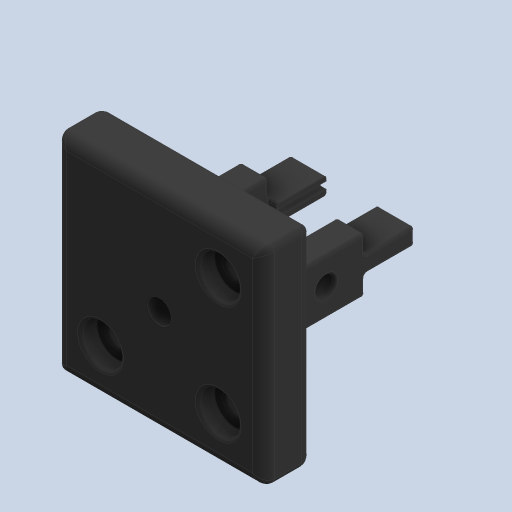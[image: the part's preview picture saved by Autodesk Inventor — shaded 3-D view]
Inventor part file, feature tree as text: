
AUTODESK INVENTOR PART (.ipt)
format: ipt  version: 2023 (Build 270158000, 158)  size: 980,992 bytes
history: native  units: mm
features: other x13, extrude x13, fillet x6, chamfer x4, sketch x3, mirror x1, projected_geometry x1
ambient origin geometry x8: Origin, YZ Plane, XZ Plane, XY Plane, X Axis, Y Axis, Z Axis, Center Point
bodies: Solid1 (feature_tree)
feature tree (41):
  other  "NP2-Alpha_Payload.ipt"
  other  "Universal_ConstructorHead.ipt"
  other  "Sk:SideArmSlot"
  extrude  "Ex:SideArmSlot"  Depth=9.0mm TaperAngle=0.0deg
  extrude  "Ex:SideArmExtension"  TaperAngle=0.0deg  [1 undecoded]
  other  "Sk:LateralFeatures"
  extrude  "Ex:TopConnection"  Depth=1.0mm
  extrude  "Ex:ThreadProtrusion"  Depth=1.0mm
  fillet  "Fillet:Protrusion"  Radius=6.5mm
  fillet  "Fillet:AllOfArm"  Radius=1.0mm
  extrude  "Ex:ScrewHole"  Depth=10.0mm
  extrude  "Ex:InterArmExtend"  Depth=1.0mm TaperAngle=0.0deg
  other  "Move:InterArmExtend"
  mirror  "Mirror1"
  extrude  "Ex:ThreadInsert"  Depth=9.0mm TaperAngle=0.0deg
  chamfer  "Chamfer:ThreadInsertOpt1"  Distance=10.0mm
  chamfer  "Chamfer:ThreadInsertOpt2"  Distance=3.0mm
  fillet  "Fillet:ThroughHoleOpt1"  Radius=6.5mm
  fillet  "Fillet:ThroughHoleOpt2"  Radius=6.5mm
  other  "TopPlane"
  other  "Sk:TopExpansion"
  fillet  "Fillet:TopCorner"  Radius=6.5mm
  extrude  "Ex:MainTopBody"  Depth=1.0mm
  extrude  "Ex:CavitiesForPosts"  Depth=10.0mm
  extrude  "Ex:TopThread1"  TaperAngle=0.0deg  [1 undecoded]
  chamfer  "Chamfer:TopThread1"  Distance=5.0mm
  extrude  "Ex:PostThroughHoles"  Depth=1.0mm TaperAngle=0.0deg
  extrude  "Ex:ScrewRecesses"  Depth=1.0mm
  extrude  "Ex:TopThread2"  TaperAngle=0.0deg  [1 undecoded]
  chamfer  "Chamfer:TopThread2"  Distance=3.0mm
  fillet  "Fillet:Final"  Radius=7.0mm
  other  "TaggingFeature1"
  other  "TaggingFeature2"
  sketch  "Sketch13"  dims[d0=10.0mm d3=9.0mm d4=0.0mm]
  sketch  "Sketch14"  dims[d21=20.0mm d22=0.0mm d51=0.0mm]
  sketch  "Sketch15"  dims[d52=0.0mm d53=3.16mm d54=1.16mm d55=6.5mm d57=1.0mm d65=10.0mm d80=6.0mm d81=0.0mm d82=9.0mm d83=0.0mm d135=10.0mm d136=0.0mm d137=3.0mm d138=0.0mm d140=6.5mm d141=6.5mm d142=6.5mm d147=5.0mm d148=10.0mm d149=0.0mm d150=5.0mm d151=15.0mm d152=0.0mm d154=8.0mm d155=0.0mm d157=3.0mm d158=7.0mm d159=0.0mm d160=3.3mm d161=0.0mm d162=0.0mm d163=5.9mm d164=5.9mm d165=2.95mm d166=2.95mm d167=0.0mm d168=0.0mm d169=4.9mm d170=3.9mm d171=0.5mm d172=4.9mm d173=20.0mm d174=0.0mm d178=0.2mm d179=2.0mm d180=45.0deg d181=0.2mm d182=2.0mm d183=45.0deg d184=4.9mm d185=0.5mm d186=2.0mm d187=0.1mm d188=10.0mm d189=10.0mm d190=2.0mm d191=3.9mm d192=5.0mm d193=0.0mm d194=0.2mm d195=2.0mm d196=45.0deg d197=10.0mm d198=2.0mm d199=1.0mm d200=0.5mm d201=10.0mm d202=10.0mm d203=3.9mm d204=5.0mm d205=0.0mm d206=0.2mm d207=2.0mm d208=45.0deg d209=0.5mm d210=4.9mm d211=0.5mm d212=4.9mm d216=0.25mm d217=0.0mm d218=0.0mm d219=-0.25mm d220=0.0mm d221=0.0mm d5=0.5mm d6=0.872665mm d97=0.5mm d98=0.872665mm d99=0.5mm d100=0.872665mm d112=1.0mm d113=1.0mm d114=6.0mm d115=0.15mm d116=3.4mm d117=0.375mm d118=14.3117mm d119=6.0mm d120=20.594885mm d121=0.0625mm d122=0.75mm d123=0.375mm d124=14.3117mm d125=0.75mm d126=20.594885mm d127=0.0625mm d128=0.75mm d129=0.375mm d139=1.0mm d143=0.25mm d144=0.375mm d145=14.3117mm d146=0.75mm]
  projected_geometry  "Projected Loop6"
  other  "Solid1::NP2-Alpha_Payload.ipt"
  other  "Srf1"
  other  "Solid1::Universal_ConstructorHead.ipt"
  other  "Srf2"
note: 3 required parameter values undecoded (feature->parameter linkage not recoverable at this tier; creation-order binding heuristic only, values carry confidence <= 0.55)
